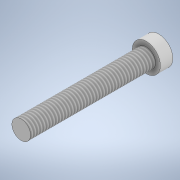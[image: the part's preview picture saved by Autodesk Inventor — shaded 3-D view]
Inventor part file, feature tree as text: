
AUTODESK INVENTOR PART (.ipt)
format: ipt  version: 2020 (Build 240168000, 168)  size: 108,032 bytes
history: native  units: in
note: dims shown in document units (in); Inventor stores cm internally (conversion verified against a paired STEP export)
features: sketch x2, extrude x2, thread x1
ambient origin geometry x8: Origin, YZ Plane, XZ Plane, XY Plane, X Axis, Y Axis, Z Axis, Center Point
bodies: Solid1 (feature_tree)
feature tree (5):
  sketch  "Sketch1"  dims[d0=0.1181in d1=0.1772in]
  extrude  "Extrusion1"  Depth=0.1772in
  extrude  "Extrusion2"  Depth=0.0787in TaperAngle=0.0deg
  thread  "Thread1"  [1 undecoded]
  sketch  "Sketch2"  dims[d2=0.1181in d3=0.1772in d4=0.7874in d5=0.0in d6=0.0787in d7=0.0in d8=0.3937in d9=0.0in]
note: 1 required parameter value undecoded (feature->parameter linkage not recoverable at this tier; creation-order binding heuristic only, values carry confidence <= 0.55)
